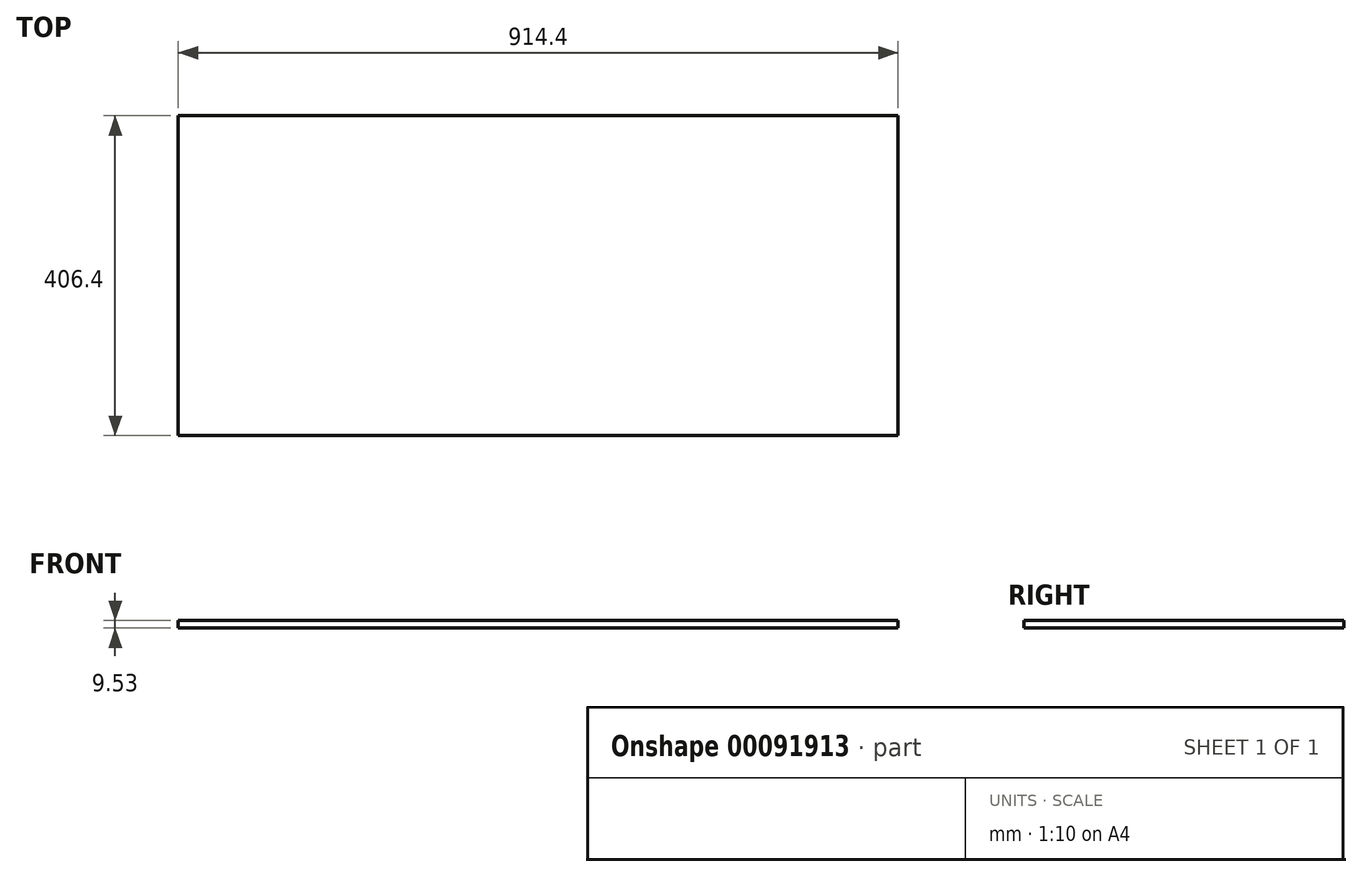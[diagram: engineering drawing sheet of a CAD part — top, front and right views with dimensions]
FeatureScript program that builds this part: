
annotation { "Feature Type Name" : "Feature", "Feature Type Description" : "" }
export const myFeature = defineFeature(function(context is Context, id is Id, definition is map)
    precondition{}
    {
        {
            var Q0;
            Q0=qCreatedBy(makeId("Top.planeOp"),FACE);
            var sketch = newSketch(context, id + "F0", { "sketchPlane" : qUnion([Q0])});
            skLineSegment(sketch, "E0.bottom", {"start": v(-457.2, -203.2) * mm, "end": v(457.2, -203.2) * mm});
            skLineSegment(sketch, "E0.top", {"start": v(-457.2, 203.2) * mm, "end": v(457.2, 203.2) * mm});
            skLineSegment(sketch, "E0.left", {"start": v(-457.2, -203.2) * mm, "end": v(-457.2, 203.2) * mm});
            skLineSegment(sketch, "E0.right", {"start": v(457.2, -203.2) * mm, "end": v(457.2, 203.2) * mm});
            skPoint(sketch, "E0.middle", {"position": v(0, 0) * mm});
            skLineSegment(sketch, "E1", {"start": v(0, 322.84) * mm, "end": v(0, -328.31) * mm, "construction": true});
            skLineSegment(sketch, "E2", {"start": v(658.45, 0) * mm, "end": v(-520.88, 0) * mm, "construction": true});
            skLineSegment(sketch, "E3", {"start": v(-505.34, 190.5) * mm, "end": v(628.67, 190.5) * mm, "construction": true});
            skLineSegment(sketch, "E4", {"start": v(444.5, 347.83) * mm, "end": v(444.5, -384.51) * mm, "construction": true});
            skLineSegment(sketch, "E5", {"start": v(628.54, -190.5) * mm, "end": v(-605.11, -190.5) * mm, "construction": true});
            skLineSegment(sketch, "E6", {"start": v(-444.5, 347.83) * mm, "end": v(-444.5, -367.08) * mm, "construction": true});
            skSolve(sketch);
        }
        {
            var Q0;
            Q0 = qSketchRegion(id + "F0", true);
            extrude(context, id + "F1", {"entities" : qUnion([Q0]), "depth" : 9.52 * mm});
        }
    });
